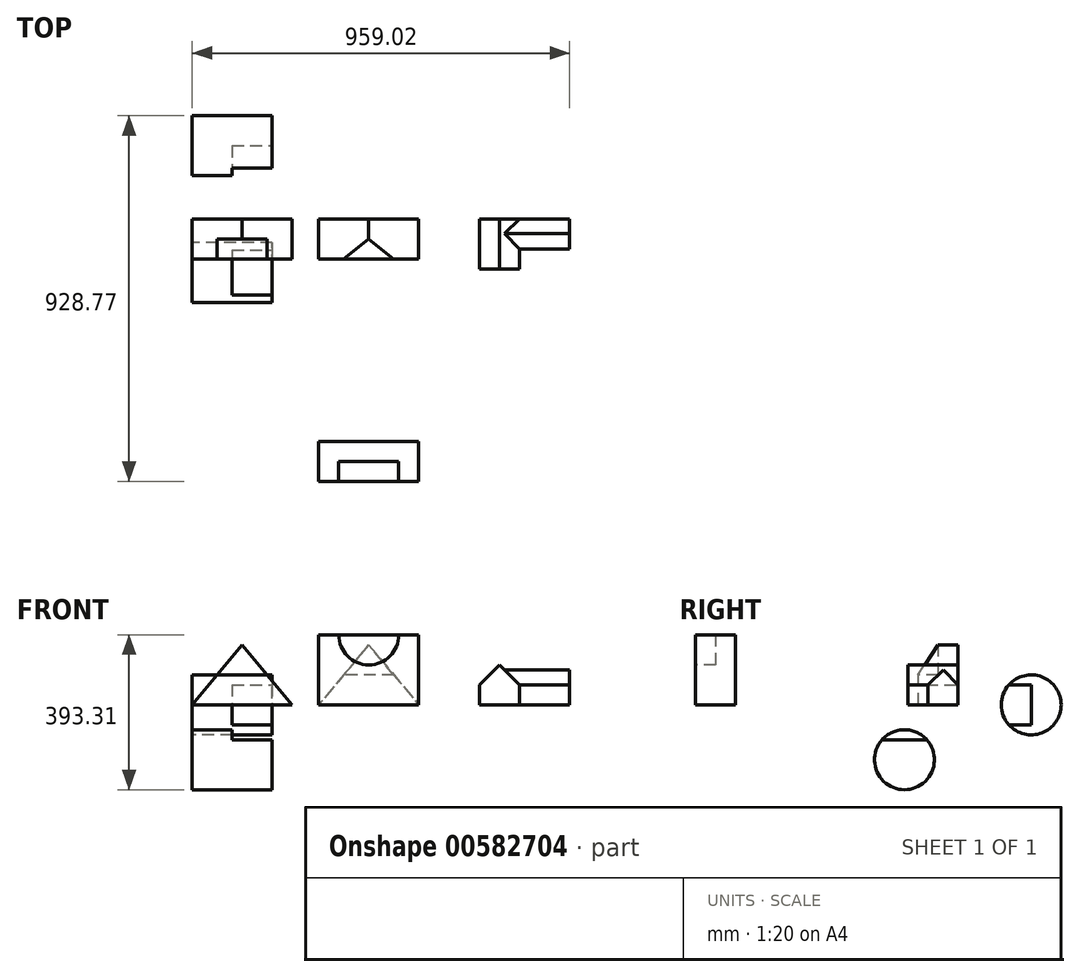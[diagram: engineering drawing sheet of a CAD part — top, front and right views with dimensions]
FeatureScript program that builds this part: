
annotation { "Feature Type Name" : "Feature", "Feature Type Description" : "" }
export const myFeature = defineFeature(function(context is Context, id is Id, definition is map)
    precondition{}
    {
        {
            var Q0;
            Q0=qCreatedBy(makeId("Front.planeOp"),FACE);
            var sketch = newSketch(context, id + "F0", { "sketchPlane" : qUnion([Q0])});
            skLineSegment(sketch, "E0", {"start": v(0, 0) * mm, "end": v(254, 0) * mm});
            skLineSegment(sketch, "E1", {"start": v(127, 152.4) * mm, "end": v(0, 0) * mm});
            skLineSegment(sketch, "E2", {"start": v(127, 152.4) * mm, "end": v(254, 0) * mm});
            skLineSegment(sketch, "E3", {"start": v(63.5, 76.2) * mm, "end": v(190.5, 76.2) * mm});
            skSolve(sketch);
        }
        {
            var Q0;
            {var subQ0=sQuery(id+"F0.wireOp",EDGE,"E0");Q0=makeQuery(id+"F0.imprint","IMPRINT",FACE,{"disambiguationData":[TD([[makeQuery(id+"F0.imprint","IMPRINT",EDGE,{"derivedFrom":subQ0}),1.0]])]});}
            var Q1;
            {var subQ3=sQuery(id+"F0.wireOp",EDGE,"E3");Q1=makeQuery(id+"F0.imprint","IMPRINT",FACE,{"disambiguationData":[TD([[makeQuery(id+"F0.imprint","IMPRINT",EDGE,{"derivedFrom":subQ3}),1.0]])]});}
            extrude(context, id + "F1", {"entities" : qUnion([Q0, Q1]), "depth" : 101.6 * mm, "offsetDistance" : 25.4 * mm});
        }
        {
            var Q0;
            Q0=makeQuery(id+"F1.opExtrude","CAP_FACE",FACE,{"disambiguationData":[OSD([sQuery(id+"F0.wireOp",EDGE,"E0"),sQuery(id+"F0.wireOp",EDGE,"E1"),sQuery(id+"F0.wireOp",EDGE,"E2")])],"isStart":false});
            var sketch = newSketch(context, id + "F2", { "sketchPlane" : qUnion([Q0])});
            skLineSegment(sketch, "E4", {"start": v(63.5, 76.2) * mm, "end": v(190.5, 76.2) * mm});
            skSolve(sketch);
        }
        {
            var Q0;
            Q0 = qSketchRegion(id + "F2", true);
            var Q1;
            {var subQ0=sQuery(id+"F2.wireOp",EDGE,"E4");Q1=makeQuery(id+"F2.imprint","IMPRINT",FACE,{"disambiguationData":[TD([[makeQuery(id+"F2.imprint","IMPRINT",EDGE,{"derivedFrom":subQ0}),1.0]])]});}
            extrude(context, id + "F3", {"entities" : qUnion([Q0, Q1]), "operationType" : NewBodyOperationType.ADD, "oppositeDirection" : true, "depth" : 50.8 * mm, "offsetDistance" : 25.4 * mm});
        }
        {
            var Q0;
            Q0=makeQuery(id+"F1.opExtrude","CAP_FACE",FACE,{"disambiguationData":[OSD([sQuery(id+"F0.wireOp",EDGE,"E0"),sQuery(id+"F0.wireOp",EDGE,"E1"),sQuery(id+"F0.wireOp",EDGE,"E2")])],"isStart":false});
            var sketch = newSketch(context, id + "F4", { "sketchPlane" : qUnion([Q0])});
            skLineSegment(sketch, "E5", {"start": v(63.5, 76.2) * mm, "end": v(190.5, 76.2) * mm});
            skSolve(sketch);
        }
        {
            var Q0;
            Q0 = qSketchRegion(id + "F4", true);
            var Q1;
            {var subQ0=sQuery(id+"F4.wireOp",EDGE,"E5");Q1=makeQuery(id+"F4.imprint","IMPRINT",FACE,{"disambiguationData":[TD([[makeQuery(id+"F4.imprint","IMPRINT",EDGE,{"derivedFrom":subQ0}),1.0]])]});}
            extrude(context, id + "F5", {"entities" : qUnion([Q0, Q1]), "operationType" : NewBodyOperationType.REMOVE, "oppositeDirection" : true, "depth" : 50.8 * mm, "offsetDistance" : 25.4 * mm});
        }
        {
            var Q0;
            Q0=qCreatedBy(makeId("Right.planeOp"),FACE);
            cPlane(context, id + "F6", {"entities" : qUnion([Q0]), "cplaneType" : CPlaneType.OFFSET, "offset" : 321.56 * mm, "width" : 152.4 * mm, "height" : 152.4 * mm});
        }
        {
            var Q0;
            Q0=qCreatedBy(id+"F6.planeOp",FACE);
            var sketch = newSketch(context, id + "F7", { "sketchPlane" : qUnion([Q0])});
            skLineSegment(sketch, "E6", {"start": v(0, 0) * mm, "end": v(0, 152.4) * mm});
            skLineSegment(sketch, "E7", {"start": v(0, 152.4) * mm, "end": v(-50.8, 152.4) * mm});
            skLineSegment(sketch, "E8", {"start": v(-50.8, 152.4) * mm, "end": v(-101.6, 76.2) * mm});
            skLineSegment(sketch, "E9", {"start": v(-101.6, 76.2) * mm, "end": v(-101.6, 0) * mm});
            skLineSegment(sketch, "E10", {"start": v(-101.6, 0) * mm, "end": v(0, 0) * mm});
            skSolve(sketch);
        }
        {
            var Q0;
            Q0 = qSketchRegion(id + "F7", true);
            extrude(context, id + "F8", {"entities" : qUnion([Q0]), "depth" : 254 * mm, "offsetDistance" : 25.4 * mm});
        }
        {
            var Q0;
            Q0=makeQuery(id+"F8.opExtrude","SWEPT_FACE",FACE,{"disambiguationData":[OSD([sQuery(id+"F7.wireOp",EDGE,"E9")])]});
            var sketch = newSketch(context, id + "F9", { "sketchPlane" : qUnion([Q0])});
            skLineSegment(sketch, "E11", {"start": v(575.56, 0) * mm, "end": v(321.56, 0) * mm});
            skLineSegment(sketch, "E12", {"start": v(448.56, 152.4) * mm, "end": v(321.56, 0) * mm});
            skLineSegment(sketch, "E13", {"start": v(448.56, 152.4) * mm, "end": v(575.56, 0) * mm});
            skLineSegment(sketch, "E14", {"start": v(448.56, 152.4) * mm, "end": v(321.56, 152.4) * mm});
            skLineSegment(sketch, "E15", {"start": v(321.56, 152.4) * mm, "end": v(321.56, 0) * mm});
            skLineSegment(sketch, "E16", {"start": v(575.56, 0) * mm, "end": v(575.56, 152.4) * mm});
            skLineSegment(sketch, "E17", {"start": v(575.56, 152.4) * mm, "end": v(448.56, 152.4) * mm});
            skSolve(sketch);
        }
        {
            var Q0;
            {var subQ0=sQuery(id+"F9.wireOp",EDGE,"E14");Q0=makeQuery(id+"F9.imprint","IMPRINT",FACE,{"disambiguationData":[TD([[makeQuery(id+"F9.imprint","IMPRINT",EDGE,{"derivedFrom":subQ0}),1.0]])]});}
            var Q1;
            {var subQ0=sQuery(id+"F9.wireOp",EDGE,"E15");var subQ1=sQuery(id+"F9.wireOp",EDGE,"E12");var subQ2=makeQuery(id+"F9.imprint","INTERSECT",VERTEX,{"derivedFrom":[sQuery(id+"F9.wireOp",EDGE,"E11"),subQ1,subQ0]});Q1=makeQuery(id+"F9.imprint","IMPRINT",FACE,{"disambiguationData":[TD([[makeQuery(id+"F9.imprint","IMPRINT",EDGE,{"disambiguationData":[TD([[subQ2,1.0]])],"derivedFrom":subQ1}),-1.0]])]});}
            var Q2;
            {var subQ0=sQuery(id+"F9.wireOp",EDGE,"E16");var subQ1=sQuery(id+"F9.wireOp",EDGE,"E13");var subQ2=makeQuery(id+"F9.imprint","INTERSECT",VERTEX,{"derivedFrom":[sQuery(id+"F9.wireOp",EDGE,"E11"),subQ1,subQ0]});Q2=makeQuery(id+"F9.imprint","IMPRINT",FACE,{"disambiguationData":[TD([[makeQuery(id+"F9.imprint","IMPRINT",EDGE,{"disambiguationData":[TD([[subQ2,1.0]])],"derivedFrom":subQ1}),1.0]])]});}
            var Q3;
            {var subQ0=sQuery(id+"F9.wireOp",EDGE,"E17");Q3=makeQuery(id+"F9.imprint","IMPRINT",FACE,{"disambiguationData":[TD([[makeQuery(id+"F9.imprint","IMPRINT",EDGE,{"derivedFrom":subQ0}),1.0]])]});}
            extrude(context, id + "F10", {"entities" : qUnion([Q0, Q1, Q2, Q3]), "operationType" : NewBodyOperationType.REMOVE, "oppositeDirection" : true, "depth" : 101.6 * mm, "offsetDistance" : 25.4 * mm});
        }
        {
            var Q0;
            Q0=qCreatedBy(makeId("Front.planeOp"),FACE);
            var sketch = newSketch(context, id + "F11", { "sketchPlane" : qUnion([Q0])});
            skLineSegment(sketch, "E18", {"start": v(730.42, 0) * mm, "end": v(730.42, 50.8) * mm});
            skLineSegment(sketch, "E19", {"start": v(832.02, 50.8) * mm, "end": v(832.02, 0) * mm});
            skLineSegment(sketch, "E20", {"start": v(832.02, 0) * mm, "end": v(730.42, 0) * mm});
            skLineSegment(sketch, "E21", {"start": v(781.22, 0) * mm, "end": v(780.45, 101.6) * mm});
            skLineSegment(sketch, "E22", {"start": v(730.42, 50.8) * mm, "end": v(780.45, 101.6) * mm});
            skLineSegment(sketch, "E23", {"start": v(780.45, 101.6) * mm, "end": v(832.02, 50.8) * mm});
            skSolve(sketch);
        }
        {
            var Q0;
            Q0 = qSketchRegion(id + "F11", true);
            extrude(context, id + "F12", {"entities" : qUnion([Q0]), "depth" : 127 * mm, "offsetDistance" : 25.4 * mm});
        }
        {
            var Q0;
            Q0=makeQuery(id+"F12.opExtrude","SWEPT_FACE",FACE,{"disambiguationData":[OSD([sQuery(id+"F11.wireOp",EDGE,"E19")])]});
            var sketch = newSketch(context, id + "F13", { "sketchPlane" : qUnion([Q0])});
            skLineSegment(sketch, "E24", {"start": v(0, 0) * mm, "end": v(0, 50.8) * mm});
            skLineSegment(sketch, "E25", {"start": v(0, 50.8) * mm, "end": v(-37.42, 89.3) * mm});
            skLineSegment(sketch, "E26", {"start": v(-37.42, 89.3) * mm, "end": v(-77.05, 50.8) * mm});
            skLineSegment(sketch, "E27", {"start": v(-77.05, 50.8) * mm, "end": v(-77.05, 0) * mm});
            skLineSegment(sketch, "E28", {"start": v(-77.05, 0) * mm, "end": v(0, 0) * mm});
            skSolve(sketch);
        }
        {
            var Q0;
            {var subQ0=sQuery(id+"F13.wireOp",EDGE,"E25");Q0=makeQuery(id+"F13.imprint","IMPRINT",FACE,{"disambiguationData":[TD([[makeQuery(id+"F13.imprint","IMPRINT",EDGE,{"derivedFrom":subQ0}),1.0]])]});}
            var Q1;
            {var subQ0=sQuery(id+"F13.wireOp",EDGE,"E24");Q1=makeQuery(id+"F13.imprint","IMPRINT",FACE,{"disambiguationData":[TD([[makeQuery(id+"F13.imprint","IMPRINT",EDGE,{"derivedFrom":subQ0}),-1.0]])]});}
            extrude(context, id + "F14", {"entities" : qUnion([Q0, Q1]), "operationType" : NewBodyOperationType.ADD, "depth" : 127 * mm, "offsetDistance" : 25.4 * mm});
        }
        {
            var Q0;
            {var subQ0=sQuery(id+"F13.wireOp",EDGE,"E25");Q0=makeQuery(id+"F13.imprint","IMPRINT",FACE,{"disambiguationData":[TD([[makeQuery(id+"F13.imprint","IMPRINT",EDGE,{"derivedFrom":subQ0}),1.0]])]});}
            extrude(context, id + "F15", {"entities" : qUnion([Q0]), "operationType" : NewBodyOperationType.ADD, "endBound" : BoundingType.UP_TO_NEXT, "oppositeDirection" : true, "depth" : 25.4 * mm, "offsetDistance" : 25.4 * mm});
        }
        {
            var Q0;
            Q0=qCreatedBy(makeId("Right.planeOp"),FACE);
            var sketch = newSketch(context, id + "F16", { "sketchPlane" : qUnion([Q0])});
            skCircle(sketch, "E29", {"center": v(-136.3, -139.31) * mm, "radius": 76.2 * mm});
            skLineSegment(sketch, "E30", {"start": v(-136.3, -139.31) * mm, "end": v(-136.3, -215.51) * mm});
            skLineSegment(sketch, "E31", {"start": v(-140.11, -88.61) * mm, "end": v(-193.18, -88.61) * mm});
            skLineSegment(sketch, "E32", {"start": v(-193.18, -88.61) * mm, "end": v(-79.42, -88.61) * mm});
            skSolve(sketch);
        }
        {
            var Q0;
            {var subQ0=sQuery(id+"F16.wireOp",EDGE,"E29");var subQ1=makeQuery(id+"F16.imprint","IMPRINT",VERTEX,{"derivedFrom":subQ0});Q0=makeQuery(id+"F16.imprint","IMPRINT",FACE,{"disambiguationData":[TD([[makeQuery(id+"F16.imprint","IMPRINT",EDGE,{"disambiguationData":[TD([[subQ1,1.0]])],"derivedFrom":subQ0}),1.0]])]});}
            var Q1;
            {var subQ0=sQuery(id+"F16.wireOp",EDGE,"E32");var subQ4=makeQuery(id+"F16.imprint","IMPRINT",VERTEX,{"derivedFrom":subQ0});Q1=makeQuery(id+"F16.imprint","IMPRINT",FACE,{"disambiguationData":[TD([[makeQuery(id+"F16.imprint","IMPRINT",EDGE,{"disambiguationData":[TD([[subQ4,1.0]])],"derivedFrom":subQ0}),1.0]])]});}
            extrude(context, id + "F17", {"entities" : qUnion([Q0, Q1]), "depth" : 203.2 * mm, "offsetDistance" : 25.4 * mm});
        }
        {
            var Q0;
            Q0=makeQuery(id+"F17.opExtrude","CAP_FACE",FACE,{"disambiguationData":[OSD([sQuery(id+"F16.wireOp",EDGE,"E29")])],"isStart":false});
            var sketch = newSketch(context, id + "F18", { "sketchPlane" : qUnion([Q0])});
            skLineSegment(sketch, "E33", {"start": v(-136.55, -88.52) * mm, "end": v(-193.1, -88.52) * mm});
            skLineSegment(sketch, "E34", {"start": v(-193.1, -88.52) * mm, "end": v(-79.5, -88.52) * mm});
            skSolve(sketch);
        }
        {
            var Q0;
            Q0 = qSketchRegion(id + "F18", true);
            var Q1;
            {var subQ0=sQuery(id+"F18.wireOp",EDGE,"E34");var subQ3=makeQuery(id+"F18.imprint","IMPRINT",VERTEX,{"derivedFrom":subQ0});Q1=makeQuery(id+"F18.imprint","IMPRINT",FACE,{"disambiguationData":[TD([[makeQuery(id+"F18.imprint","IMPRINT",EDGE,{"disambiguationData":[TD([[subQ3,1.0]])],"derivedFrom":subQ0}),1.0]])]});}
            extrude(context, id + "F19", {"entities" : qUnion([Q0, Q1]), "operationType" : NewBodyOperationType.ADD, "oppositeDirection" : true, "depth" : 101.6 * mm, "offsetDistance" : 25.4 * mm});
        }
        {
            var Q0;
            {var subQ0=sQuery(id+"F18.wireOp",EDGE,"E34");var subQ3=makeQuery(id+"F18.imprint","IMPRINT",VERTEX,{"derivedFrom":subQ0});Q0=makeQuery(id+"F18.imprint","IMPRINT",FACE,{"disambiguationData":[TD([[makeQuery(id+"F18.imprint","IMPRINT",EDGE,{"disambiguationData":[TD([[subQ3,1.0]])],"derivedFrom":subQ0}),1.0]])]});}
            extrude(context, id + "F20", {"entities" : qUnion([Q0]), "operationType" : NewBodyOperationType.REMOVE, "oppositeDirection" : true, "depth" : 101.6 * mm, "offsetDistance" : 25.4 * mm});
        }
        {
            var Q0;
            Q0=qCreatedBy(makeId("Right.planeOp"),FACE);
            var sketch = newSketch(context, id + "F21", { "sketchPlane" : qUnion([Q0])});
            skCircle(sketch, "E35", {"center": v(185.84, 0) * mm, "radius": 76.2 * mm});
            skLineSegment(sketch, "E36", {"start": v(185.84, 0) * mm, "end": v(185.84, 76.2) * mm});
            skSolve(sketch);
        }
        {
            var Q0;
            Q0 = qSketchRegion(id + "F21", true);
            extrude(context, id + "F22", {"entities" : qUnion([Q0]), "depth" : 203.2 * mm, "offsetDistance" : 25.4 * mm});
        }
        {
            var Q0;
            Q0=makeQuery(id+"F22.opExtrude","CAP_FACE",FACE,{"disambiguationData":[OSD([sQuery(id+"F21.wireOp",EDGE,"E35")])],"isStart":false});
            var sketch = newSketch(context, id + "F23", { "sketchPlane" : qUnion([Q0])});
            skLineSegment(sketch, "E37", {"start": v(109.64, 0) * mm, "end": v(185.84, 0) * mm});
            skLineSegment(sketch, "E38", {"start": v(185.84, -50.8) * mm, "end": v(129.05, -50.8) * mm});
            skLineSegment(sketch, "E39", {"start": v(185.84, 50.8) * mm, "end": v(129.05, 50.8) * mm});
            skLineSegment(sketch, "E40", {"start": v(185.84, 50.8) * mm, "end": v(185.84, -50.8) * mm});
            skSolve(sketch);
        }
        {
            var Q0;
            Q0 = qSketchRegion(id + "F23", true);
            var Q1;
            {var subQ0=sQuery(id+"F23.wireOp",EDGE,"E37");Q1=makeQuery(id+"F23.imprint","IMPRINT",FACE,{"disambiguationData":[TD([[makeQuery(id+"F23.imprint","IMPRINT",EDGE,{"derivedFrom":subQ0}),1.0]])]});}
            var Q2;
            {var subQ0=sQuery(id+"F23.wireOp",EDGE,"E37");Q2=makeQuery(id+"F23.imprint","IMPRINT",FACE,{"disambiguationData":[TD([[makeQuery(id+"F23.imprint","IMPRINT",EDGE,{"derivedFrom":subQ0}),-1.0]])]});}
            extrude(context, id + "F24", {"entities" : qUnion([Q0, Q1, Q2]), "operationType" : NewBodyOperationType.REMOVE, "oppositeDirection" : true, "depth" : 101.6 * mm, "offsetDistance" : 25.4 * mm});
        }
        {
            var Q0;
            Q0=qCreatedBy(id+"F6.planeOp",FACE);
            var sketch = newSketch(context, id + "F25", { "sketchPlane" : qUnion([Q0])});
            skLineSegment(sketch, "E41", {"start": v(-666.73, 0) * mm, "end": v(-666.73, 177.8) * mm});
            skLineSegment(sketch, "E42", {"start": v(-666.73, 177.8) * mm, "end": v(-565.13, 177.8) * mm});
            skLineSegment(sketch, "E43", {"start": v(-565.13, 177.8) * mm, "end": v(-565.13, 0) * mm});
            skLineSegment(sketch, "E44", {"start": v(-565.13, 0) * mm, "end": v(-666.73, 0) * mm});
            skSolve(sketch);
        }
        {
            var Q0;
            Q0 = qSketchRegion(id + "F25", true);
            extrude(context, id + "F26", {"entities" : qUnion([Q0]), "depth" : 254 * mm, "offsetDistance" : 25.4 * mm});
        }
        {
            var Q0;
            Q0=makeQuery(id+"F26.opExtrude","SWEPT_FACE",FACE,{"disambiguationData":[OSD([sQuery(id+"F25.wireOp",EDGE,"E41")])]});
            var sketch = newSketch(context, id + "F27", { "sketchPlane" : qUnion([Q0])});
            skLineSegment(sketch, "E45", {"start": v(321.56, 177.8) * mm, "end": v(372.36, 177.8) * mm});
            skLineSegment(sketch, "E46", {"start": v(575.56, 177.8) * mm, "end": v(524.76, 177.8) * mm});
            skLineSegment(sketch, "E47", {"start": v(448.56, 177.8) * mm, "end": v(448.56, 101.6) * mm});
            skArc(sketch, "E48", {"start": v(372.36, 177.8) * mm, "mid": v(448.56, 101.6) * mm, "end": v(524.76, 177.8) * mm});
            skSolve(sketch);
        }
        {
            var Q0;
            Q0 = qSketchRegion(id + "F27", true);
            var Q1;
            {var subQ0=sQuery(id+"F27.wireOp",EDGE,"E47");Q1=makeQuery(id+"F27.imprint","IMPRINT",FACE,{"disambiguationData":[TD([[makeQuery(id+"F27.imprint","IMPRINT",EDGE,{"derivedFrom":subQ0}),1.0]])]});}
            var Q2;
            {var subQ0=sQuery(id+"F27.wireOp",EDGE,"E47");Q2=makeQuery(id+"F27.imprint","IMPRINT",FACE,{"disambiguationData":[TD([[makeQuery(id+"F27.imprint","IMPRINT",EDGE,{"derivedFrom":subQ0}),-1.0]])]});}
            extrude(context, id + "F28", {"entities" : qUnion([Q0, Q1, Q2]), "operationType" : NewBodyOperationType.REMOVE, "oppositeDirection" : true, "depth" : 50.8 * mm, "offsetDistance" : 25.4 * mm});
        }
    });
